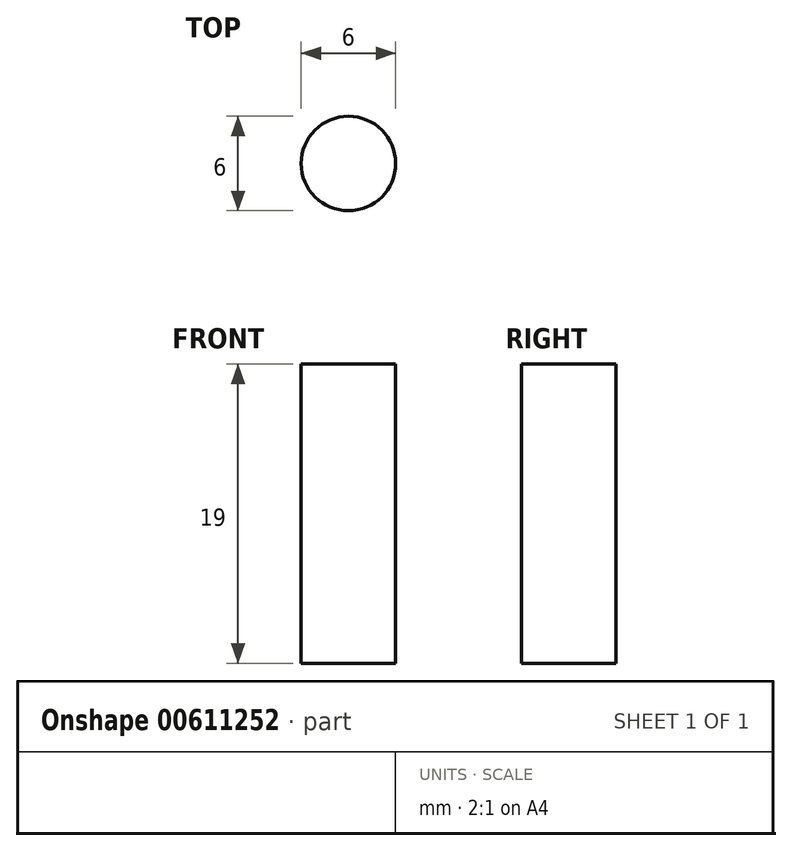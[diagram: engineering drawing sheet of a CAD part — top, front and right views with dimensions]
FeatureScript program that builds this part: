
annotation { "Feature Type Name" : "Feature", "Feature Type Description" : "" }
export const myFeature = defineFeature(function(context is Context, id is Id, definition is map)
    precondition{}
    {
        {
            var Q0;
            Q0=qCreatedBy(makeId("Top.planeOp"),FACE);
            var sketch = newSketch(context, id + "F0", { "sketchPlane" : qUnion([Q0])});
            skCircle(sketch, "E0", {"center": v(0, 0) * mm, "radius": 3 * mm});
            skSolve(sketch);
        }
        {
            var Q0;
            Q0=makeQuery(id+"F0.imprint","IMPRINT",FACE,{"disambiguationData":[TD([[makeQuery(id+"F0.imprint","IMPRINT",EDGE,{"derivedFrom":sQuery(id+"F0.wireOp",EDGE,"E0")}),1.0]])]});
            extrude(context, id + "F1", {"entities" : qUnion([Q0]), "depth" : 19 * mm, "offsetDistance" : 25 * mm});
        }
    });
